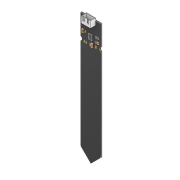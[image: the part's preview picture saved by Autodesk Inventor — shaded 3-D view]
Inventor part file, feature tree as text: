
AUTODESK INVENTOR PART (.ipt)
format: ipt  version: 2021 (Build 250183000, 183)  size: 438,272 bytes
history: native  units: mm
features: other x72, mirror x4
ambient origin geometry x8: Origin, YZ Plane, XZ Plane, XY Plane, X Axis, Y Axis, Z Axis, Center Point
bodies: Body1 (feature_tree), Body2 (feature_tree), Body3 (feature_tree), Body4 (feature_tree), Body5 (feature_tree), Body6 (feature_tree), Body7 (feature_tree), Body8 (feature_tree), Body9 (feature_tree), Body10 (feature_tree), Body11 (feature_tree), Body12 (feature_tree), Body13 (feature_tree), Body14 (feature_tree), Body15 (feature_tree), Body16 (feature_tree), Body17 (feature_tree), Body18 (feature_tree), Body19 (feature_tree), Body20 (feature_tree), Body21 (feature_tree), Body22 (feature_tree), Body23 (feature_tree), Body24 (feature_tree), Body25 (feature_tree)
feature tree (76):
  other  "Твердое тело1"
  other  "Непосредственное редактирование1"
  other  "Непосредственное редактирование2"
  other  "Непосредственное редактирование3"
  other  "Непосредственное редактирование4"
  other  "Непосредственное редактирование5"
  other  "Непосредственное редактирование6"
  other  "Непосредственное редактирование7"
  other  "Непосредственное редактирование8"
  other  "Непосредственное редактирование9"
  other  "РабПлоскость1"
  other  "Твердое тело2"
  other  "Твердое тело3"
  other  "Твердое тело4"
  other  "Твердое тело5"
  other  "Твердое тело6"
  other  "Твердое тело7"
  other  "Твердое тело8"
  other  "Твердое тело9"
  other  "Твердое тело10"
  other  "Твердое тело11"
  other  "Твердое тело12"
  other  "Твердое тело13"
  other  "Твердое тело14"
  other  "Твердое тело15"
  other  "Твердое тело16"
  other  "Твердое тело17"
  other  "Твердое тело18"
  other  "Твердое тело19"
  other  "Твердое тело20"
  other  "Твердое тело21"
  other  "Твердое тело22"
  other  "Твердое тело23"
  other  "Твердое тело24"
  other  "Твердое тело25"
  other  "Твердое тело26"
  other  "Boss-Extrude1"
  other  "Boss-Extrude2"
  other  "Boss-Extrude3[1]"
  other  "Boss-Extrude4"
  other  "Boss-Extrude5[1]"
  other  "Boss-Extrude5[2]"
  other  "Boss-Extrude5[3]"
  other  "Boss-Extrude5[4]"
  other  "Boss-Extrude6"
  other  "Boss-Extrude7"
  other  "Boss-Extrude3[2]"
  other  "Boss-Extrude3[3]"
  other  "Boss-Extrude3[4]"
  other  "Cut-Extrude1"
  other  "Boss-Extrude9[1]"
  other  "Boss-Extrude9[2]"
  other  "Boss-Extrude9[3]"
  other  "Boss-Extrude10[1]"
  other  "Boss-Extrude10[2]"
  other  "Boss-Extrude10[3]"
  other  "Boss-Extrude10[4]"
  mirror  "Mirror1[1]"
  mirror  "Mirror1[2]"
  mirror  "Mirror1[3]"
  mirror  "Mirror1[4]"
  other  "Масштаб1"
  other  "Масштаб2"
  other  "Масштаб3"
  other  "Масштаб4"
  other  "Размер1"
  other  "Размер2"
  other  "Размер3"
  other  "Размер4"
  other  "Размер5"
  other  "Размер6"
  other  "Размер7"
  other  "Размер8"
  other  "Размер9"
  other  "Размер10"
  other  "Размер11"
